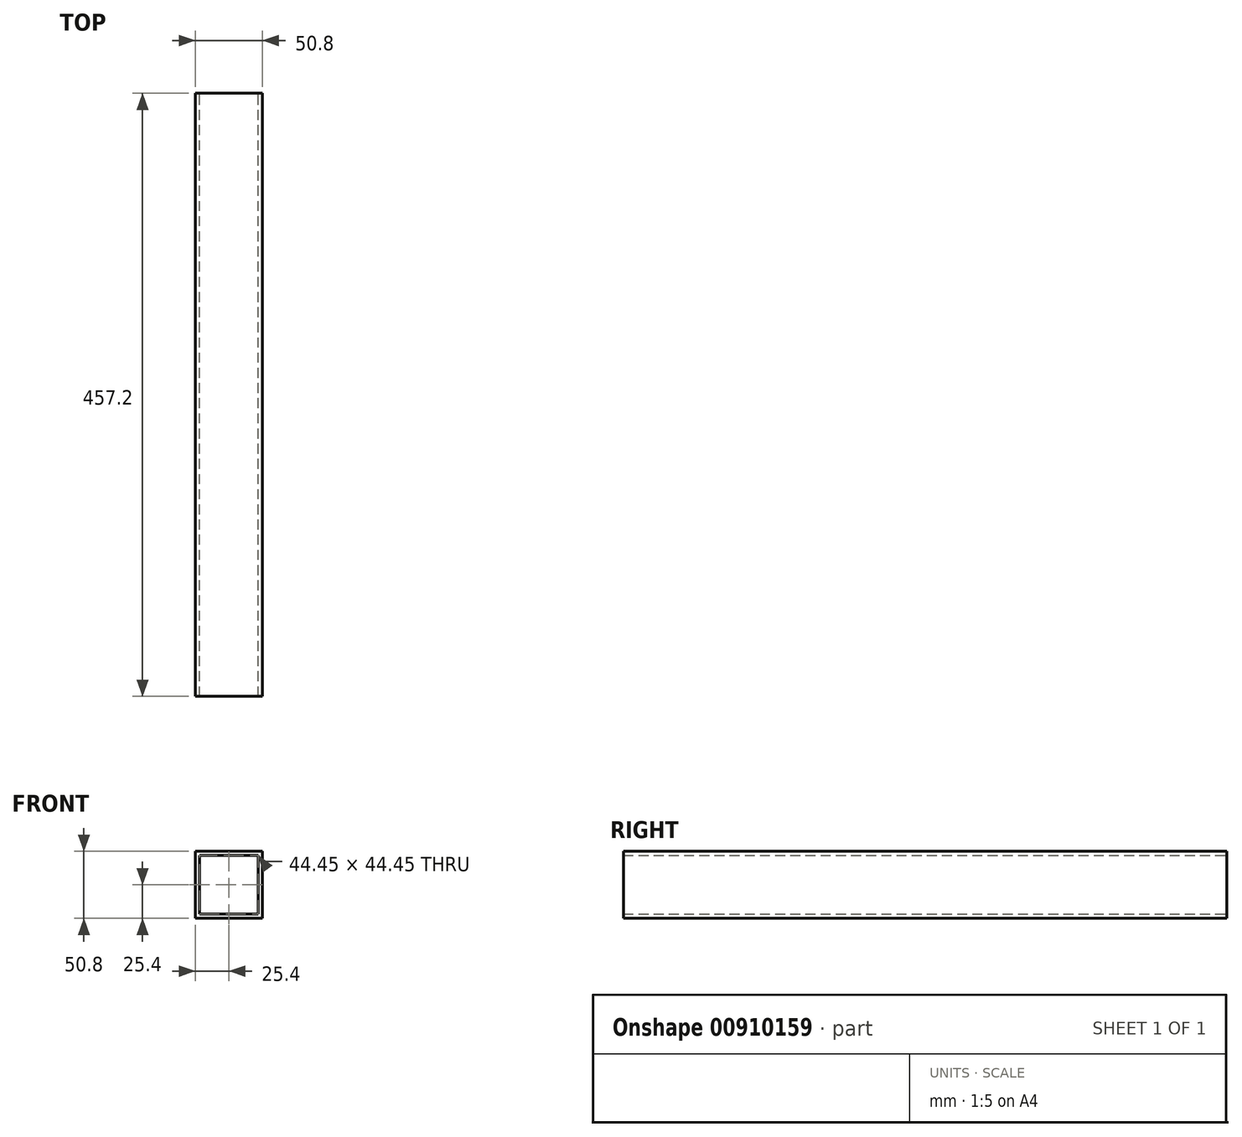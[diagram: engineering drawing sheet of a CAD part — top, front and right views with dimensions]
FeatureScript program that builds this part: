
annotation { "Feature Type Name" : "Feature", "Feature Type Description" : "" }
export const myFeature = defineFeature(function(context is Context, id is Id, definition is map)
    precondition{}
    {
        {
            var Q0;
            Q0=qCreatedBy(makeId("Right.planeOp"),FACE);
            var sketch = newSketch(context, id + "F0", { "sketchPlane" : qUnion([Q0])});
            skLineSegment(sketch, "E0.bottom", {"start": v(-228.6, 25.4) * mm, "end": v(228.6, 25.4) * mm});
            skLineSegment(sketch, "E0.top", {"start": v(-228.6, -25.4) * mm, "end": v(228.6, -25.4) * mm});
            skLineSegment(sketch, "E0.left", {"start": v(-228.6, 25.4) * mm, "end": v(-228.6, -25.4) * mm});
            skLineSegment(sketch, "E0.right", {"start": v(228.6, 25.4) * mm, "end": v(228.6, -25.4) * mm});
            skPoint(sketch, "E0.middle", {"position": v(0, 0) * mm});
            skPoint(sketch, "E1", {"position": v(207.65, 25.4) * mm});
            skPoint(sketch, "E2", {"position": v(-207.65, 25.4) * mm});
            skSolve(sketch);
        }
        {
            var Q0;
            Q0=makeQuery(id+"F0.imprint","IMPRINT",FACE,{"disambiguationData":[TD([[makeQuery(id+"F0.imprint","IMPRINT",EDGE,{"derivedFrom":sQuery(id+"F0.wireOp",EDGE,"E0.bottom")}),-1.0]])]});
            extrude(context, id + "F1", {"entities" : qUnion([Q0]), "endBound" : BoundingType.SYMMETRIC, "depth" : 50.8 * mm, "offsetDistance" : 25.4 * mm});
        }
        {
            var Q0;
            Q0=makeQuery(id+"F1.opExtrude","SWEPT_FACE",FACE,{"disambiguationData":[OSD([sQuery(id+"F0.wireOp",EDGE,"E0.left")])]});
            var Q1;
            Q1=makeQuery(id+"F1.opExtrude","SWEPT_FACE",FACE,{"disambiguationData":[OSD([sQuery(id+"F0.wireOp",EDGE,"E0.right")])]});
            shell(context, id + "F2", {"entities" : qUnion([Q0, Q1]), "thickness" : 3.17 * mm});
        }
    });
